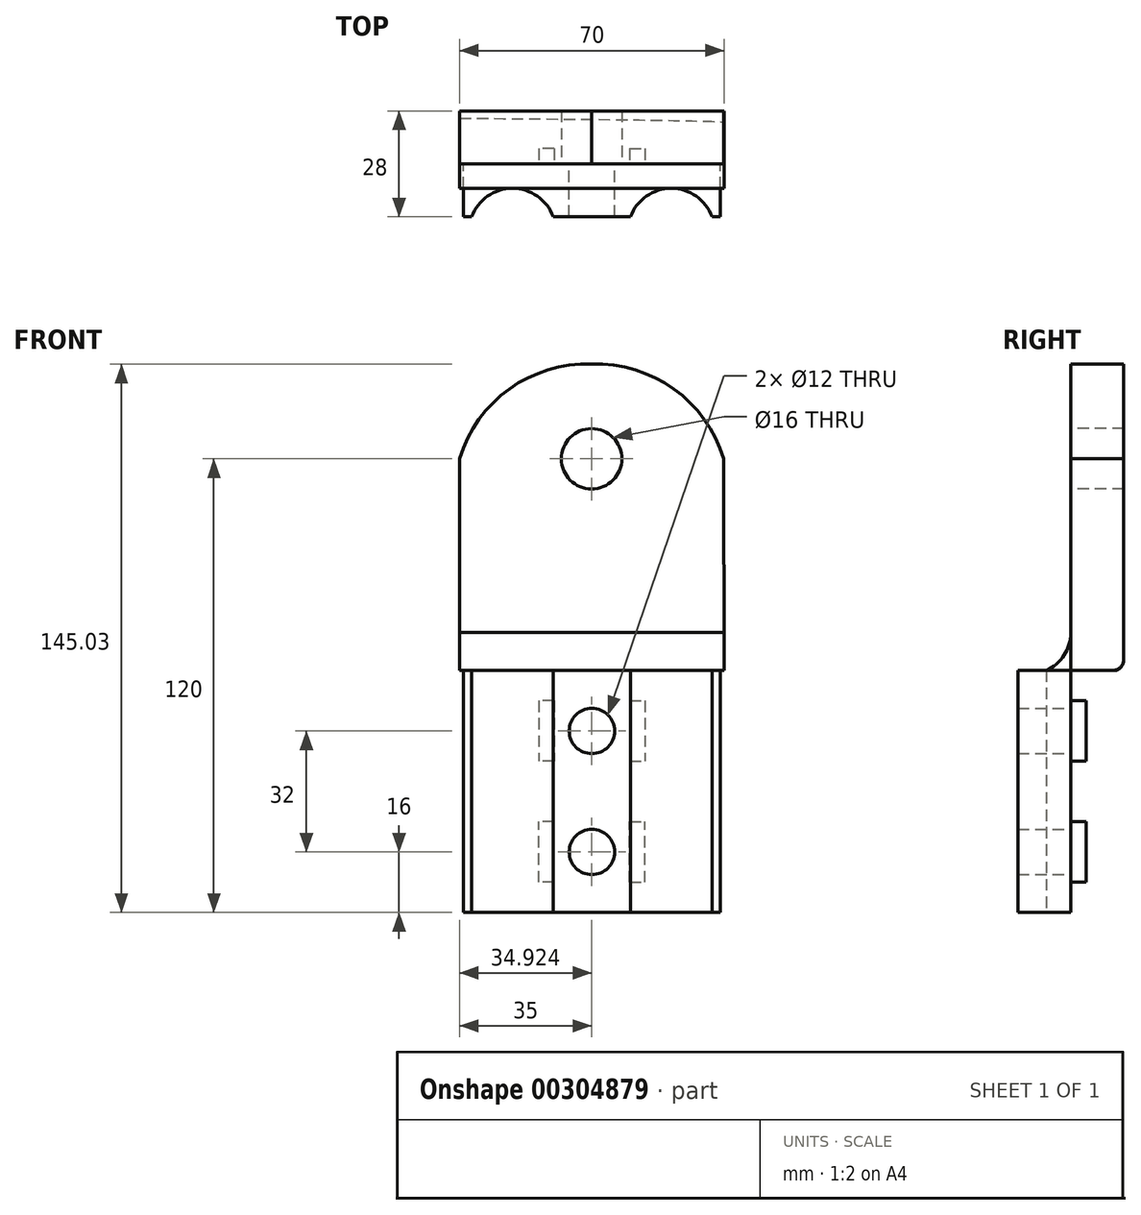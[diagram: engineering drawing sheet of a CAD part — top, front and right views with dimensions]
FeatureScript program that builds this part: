
annotation { "Feature Type Name" : "Feature", "Feature Type Description" : "" }
export const myFeature = defineFeature(function(context is Context, id is Id, definition is map)
    precondition{}
    {
        {
            var Q0;
            Q0=qCreatedBy(makeId("Front.planeOp"),FACE);
            var sketch = newSketch(context, id + "F0", { "sketchPlane" : qUnion([Q0])});
            skLineSegment(sketch, "E0.bottom", {"start": v(0, 0) * mm, "end": v(-68, 0) * mm});
            skLineSegment(sketch, "E1.MirrorCS", {"start": v(-68, 0) * mm, "end": v(-68, -64) * mm});
            skLineSegment(sketch, "E2.MirrorCS", {"start": v(0, -64) * mm, "end": v(-68, -64) * mm});
            skLineSegment(sketch, "E3.MirrorCS", {"start": v(0, 0) * mm, "end": v(0, -64) * mm});
            skLineSegment(sketch, "E4", {"start": v(0, 0) * mm, "end": v(0, -10.57) * mm});
            skLineSegment(sketch, "E5", {"start": v(-68, 0) * mm, "end": v(-68, -10.57) * mm});
            skCircle(sketch, "E6", {"center": v(-34, -48) * mm, "radius": 6 * mm});
            skPoint(sketch, "E6.centerSnap0", {"position": v(-34, -64) * mm});
            skCircle(sketch, "E7", {"center": v(-34, -16) * mm, "radius": 6 * mm});
            skPoint(sketch, "E8.end.orphan", {"position": v(-13.13, -48) * mm});
            skPoint(sketch, "E8.start.orphan", {"position": v(-13.13, -64) * mm});
            skSolve(sketch);
        }
        {
            var Q0;
            Q0=qCreatedBy(makeId("Front.planeOp"),FACE);
            var sketch = newSketch(context, id + "F1", { "sketchPlane" : qUnion([Q0])});
            skLineSegment(sketch, "E9", {"start": v(-31.33, 81) * mm, "end": v(-36.83, 81) * mm});
            skLineSegment(sketch, "E10", {"start": v(-69, 56) * mm, "end": v(-69, 0) * mm});
            skLineSegment(sketch, "E11", {"start": v(-68.15, 0) * mm, "end": v(0, 0) * mm});
            skLineSegment(sketch, "E12", {"start": v(0, 0) * mm, "end": v(0, 10) * mm});
            skLineSegment(sketch, "E13", {"start": v(-34.08, 10) * mm, "end": v(-34.08, 56) * mm});
            skPoint(sketch, "E13.startSnap0", {"position": v(-34.08, 0) * mm});
            skLineSegment(sketch, "E14", {"start": v(-69, 0) * mm, "end": v(-68, 0) * mm});
            skCircle(sketch, "E15", {"center": v(-34.08, 56) * mm, "radius": 8 * mm});
            skArc(sketch, "E16", {"start": v(-34.08, 81) * mm, "mid": v(-55.82, 74.49) * mm, "end": v(-69, 56) * mm});
            skArc(sketch, "E17.MirrorCS", {"start": v(-34.08, 81) * mm, "mid": v(-12.33, 74.49) * mm, "end": v(0.85, 56) * mm});
            skPoint(sketch, "E18.end.orphan", {"position": v(1, 81) * mm});
            skLineSegment(sketch, "E19", {"start": v(0.85, 56) * mm, "end": v(1, 0) * mm});
            skLineSegment(sketch, "E20", {"start": v(1, 0) * mm, "end": v(-4.04, 0) * mm});
            skSolve(sketch);
        }
        {
            var Q0;
            Q0 = qSketchRegion(id + "F1", true);
            extrude(context, id + "F2", {"entities" : qUnion([Q0]), "oppositeDirection" : true, "depth" : 14 * mm});
        }
        {
            var Q0;
            Q0=makeQuery(id+"F0.imprint","IMPRINT",FACE,{"disambiguationData":[TD([[makeQuery(id+"F0.imprint","IMPRINT",EDGE,{"derivedFrom":sQuery(id+"F0.wireOp",EDGE,"E0.bottom")}),1.0]])]});
            extrude(context, id + "F3", {"entities" : qUnion([Q0]), "depth" : 14 * mm});
        }
        {
            var Q0;
            Q0=makeQuery(id+"F3.opExtrude","SWEPT_FACE",FACE,{"disambiguationData":[OSD([sQuery(id+"F0.wireOp",EDGE,"E2.MirrorCS")])]});
            var sketch = newSketch(context, id + "F4", { "sketchPlane" : qUnion([Q0])});
            skPoint(sketch, "E21.startSnap0", {"position": v(-34, 18) * mm});
            skCircle(sketch, "E22", {"center": v(-55, 18) * mm, "radius": 11.5 * mm});
            skCircle(sketch, "E23", {"center": v(-13, 18) * mm, "radius": 11.5 * mm});
            skPoint(sketch, "E24.orphan", {"position": v(-55, 26.92) * mm});
            skPoint(sketch, "E25.orphan", {"position": v(-34, 26.92) * mm});
            skPoint(sketch, "E21.end.orphan", {"position": v(-13, 26.92) * mm});
            skPoint(sketch, "E26.orphan", {"position": v(-68, 18) * mm});
            skPoint(sketch, "E27.start.orphan", {"position": v(0, 18) * mm});
            skSolve(sketch);
        }
        {
            var Q0;
            {var subQ0=sQuery(id+"F4.wireOp",EDGE,"E22");var subQ1=makeQuery(id+"F3.opExtrude","CAP_EDGE",EDGE,{"disambiguationData":[OSD([sQuery(id+"F0.wireOp",EDGE,"E2.MirrorCS")])],"isStart":false});var subQ2=makeQuery(id+"F4.imprint","INTERSECT",VERTEX,{"disambiguationData":[OD(0.0)],"derivedFrom":[subQ1,subQ0]});Q0=makeQuery(id+"F4.imprint","IMPRINT",FACE,{"disambiguationData":[TD([[makeQuery(id+"F4.imprint","IMPRINT",EDGE,{"disambiguationData":[TD([[subQ2,-1.0]])],"derivedFrom":subQ0}),1.0]])]});}
            var Q1;
            {var subQ0=sQuery(id+"F4.wireOp",EDGE,"E23");var subQ1=makeQuery(id+"F3.opExtrude","CAP_EDGE",EDGE,{"disambiguationData":[OSD([sQuery(id+"F0.wireOp",EDGE,"E2.MirrorCS")])],"isStart":false});var subQ2=makeQuery(id+"F4.imprint","INTERSECT",VERTEX,{"disambiguationData":[OD(0.0)],"derivedFrom":[subQ1,subQ0]});Q1=makeQuery(id+"F4.imprint","IMPRINT",FACE,{"disambiguationData":[TD([[makeQuery(id+"F4.imprint","IMPRINT",EDGE,{"disambiguationData":[TD([[subQ2,1.0]])],"derivedFrom":subQ0}),1.0]])]});}
            extrude(context, id + "F5", {"entities" : qUnion([Q0, Q1]), "operationType" : NewBodyOperationType.REMOVE, "oppositeDirection" : true, "depth" : 64 * mm});
        }
        {
            var Q0;
            Q0=makeQuery(id+"F3.opExtrude","CAP_FACE",FACE,{"disambiguationData":[OSD([sQuery(id+"F0.wireOp",EDGE,"E0.bottom"),sQuery(id+"F0.wireOp",EDGE,"E1.MirrorCS"),sQuery(id+"F0.wireOp",EDGE,"E2.MirrorCS"),sQuery(id+"F0.wireOp",EDGE,"E3.MirrorCS"),sQuery(id+"F0.wireOp",EDGE,"E4"),sQuery(id+"F0.wireOp",EDGE,"E5"),sQuery(id+"F0.wireOp",EDGE,"E6"),sQuery(id+"F0.wireOp",EDGE,"E7")])],"isStart":true});
            var sketch = newSketch(context, id + "F6", { "sketchPlane" : qUnion([Q0])});
            skPoint(sketch, "E28.startSnap0", {"position": v(34, -64) * mm});
            skLineSegment(sketch, "E29.bottom", {"start": v(24, -56) * mm, "end": v(20, -56) * mm});
            skLineSegment(sketch, "E29.top", {"start": v(24, -40) * mm, "end": v(20, -40) * mm});
            skLineSegment(sketch, "E29.left", {"start": v(24, -56) * mm, "end": v(24, -40) * mm});
            skLineSegment(sketch, "E29.right", {"start": v(20, -56) * mm, "end": v(20, -40) * mm});
            skLineSegment(sketch, "E30.MirrorCS", {"start": v(44, -56) * mm, "end": v(44, -40) * mm});
            skLineSegment(sketch, "E31.MirrorCS", {"start": v(44, -40) * mm, "end": v(48, -40) * mm});
            skLineSegment(sketch, "E32.MirrorCS", {"start": v(48, -56) * mm, "end": v(48, -40) * mm});
            skLineSegment(sketch, "E33.MirrorCS", {"start": v(44, -56) * mm, "end": v(48, -56) * mm});
            skLineSegment(sketch, "E34.MirrorCS", {"start": v(24, -24) * mm, "end": v(20, -24) * mm});
            skLineSegment(sketch, "E35.MirrorCS", {"start": v(20, -8) * mm, "end": v(20, -24) * mm});
            skLineSegment(sketch, "E36.MirrorCS", {"start": v(24, -8) * mm, "end": v(20, -8) * mm});
            skLineSegment(sketch, "E37.MirrorCS", {"start": v(24, -8) * mm, "end": v(24, -24) * mm});
            skLineSegment(sketch, "E38.MirrorCS", {"start": v(44, -8) * mm, "end": v(44, -24) * mm});
            skLineSegment(sketch, "E39.MirrorCS", {"start": v(44, -24) * mm, "end": v(48, -24) * mm});
            skLineSegment(sketch, "E40.MirrorCS", {"start": v(48, -8) * mm, "end": v(48, -24) * mm});
            skLineSegment(sketch, "E41.MirrorCS", {"start": v(44, -8) * mm, "end": v(48, -8) * mm});
            skPoint(sketch, "E42.orphan", {"position": v(0, -32) * mm});
            skPoint(sketch, "E43.end.orphan", {"position": v(68, -32) * mm});
            skPoint(sketch, "E43.start.orphan", {"position": v(34, -32) * mm});
            skPoint(sketch, "E28.end.orphan", {"position": v(24, -68.55) * mm});
            skPoint(sketch, "E28.start.orphan", {"position": v(34, -68.55) * mm});
            skPoint(sketch, "E44.end.orphan", {"position": v(4.3, -56) * mm});
            skPoint(sketch, "E44.start.orphan", {"position": v(4.3, -64) * mm});
            skSolve(sketch);
        }
        {
            var Q0;
            Q0=makeQuery(id+"F6.imprint","IMPRINT",FACE,{"disambiguationData":[TD([[makeQuery(id+"F6.imprint","IMPRINT",EDGE,{"derivedFrom":sQuery(id+"F6.wireOp",EDGE,"E38.MirrorCS")}),1.0]])]});
            var Q1;
            Q1=makeQuery(id+"F6.imprint","IMPRINT",FACE,{"disambiguationData":[TD([[makeQuery(id+"F6.imprint","IMPRINT",EDGE,{"derivedFrom":sQuery(id+"F6.wireOp",EDGE,"E34.MirrorCS")}),-1.0]])]});
            var Q2;
            Q2=makeQuery(id+"F6.imprint","IMPRINT",FACE,{"disambiguationData":[TD([[makeQuery(id+"F6.imprint","IMPRINT",EDGE,{"derivedFrom":sQuery(id+"F6.wireOp",EDGE,"E29.bottom")}),-1.0]])]});
            var Q3;
            Q3=makeQuery(id+"F6.imprint","IMPRINT",FACE,{"disambiguationData":[TD([[makeQuery(id+"F6.imprint","IMPRINT",EDGE,{"derivedFrom":sQuery(id+"F6.wireOp",EDGE,"E30.MirrorCS")}),-1.0]])]});
            extrude(context, id + "F7", {"entities" : qUnion([Q0, Q1, Q2, Q3]), "operationType" : NewBodyOperationType.ADD, "depth" : 4 * mm});
        }
        {
            var Q0;
            Q0=makeQuery(id+"F2.opExtrude","SWEPT_FACE",FACE,{"disambiguationData":[OSD([sQuery(id+"F1.wireOp",EDGE,"E10")])]});
            var sketch = newSketch(context, id + "F8", { "sketchPlane" : qUnion([Q0])});
            skLineSegment(sketch, "E45", {"start": v(0, 0) * mm, "end": v(0, 10) * mm});
            skLineSegment(sketch, "E46", {"start": v(0, 0) * mm, "end": v(6.5, 0) * mm});
            skArc(sketch, "E47", {"start": v(0, 10) * mm, "mid": v(1.77, 4.04) * mm, "end": v(6.5, 0) * mm});
            skSolve(sketch);
        }
        {
            var Q0;
            Q0=makeQuery(id+"F8.imprint","IMPRINT",FACE,{"disambiguationData":[TD([[makeQuery(id+"F8.imprint","IMPRINT",EDGE,{"derivedFrom":sQuery(id+"F8.wireOp",EDGE,"E45")}),1.0]])]});
            extrude(context, id + "F9", {"entities" : qUnion([Q0]), "oppositeDirection" : true, "depth" : 70 * mm});
        }
        {
            var Q0;
            Q0=makeQuery(id+"F2.opExtrude","SWEPT_FACE",FACE,{"disambiguationData":[OSD([sQuery(id+"F1.wireOp",EDGE,"E19")])]});
            var sketch = newSketch(context, id + "F10", { "sketchPlane" : qUnion([Q0])});
            skLineSegment(sketch, "E48", {"start": v(14, 56) * mm, "end": v(14, 59) * mm});
            skLineSegment(sketch, "E49", {"start": v(14, 0) * mm, "end": v(14, 3) * mm});
            skLineSegment(sketch, "E50", {"start": v(14, 0) * mm, "end": v(11, 0) * mm});
            skArc(sketch, "E51", {"start": v(11, 0) * mm, "mid": v(13.12, 0.88) * mm, "end": v(14, 3) * mm});
            skSolve(sketch);
        }
        {
            var Q0;
            Q0=makeQuery(id+"F10.imprint","IMPRINT",FACE,{"disambiguationData":[TD([[makeQuery(id+"F10.imprint","IMPRINT",EDGE,{"derivedFrom":sQuery(id+"F10.wireOp",EDGE,"E49")}),-1.0]])]});
            extrude(context, id + "F11", {"entities" : qUnion([Q0]), "operationType" : NewBodyOperationType.REMOVE, "oppositeDirection" : true, "depth" : 70 * mm});
        }
    });
